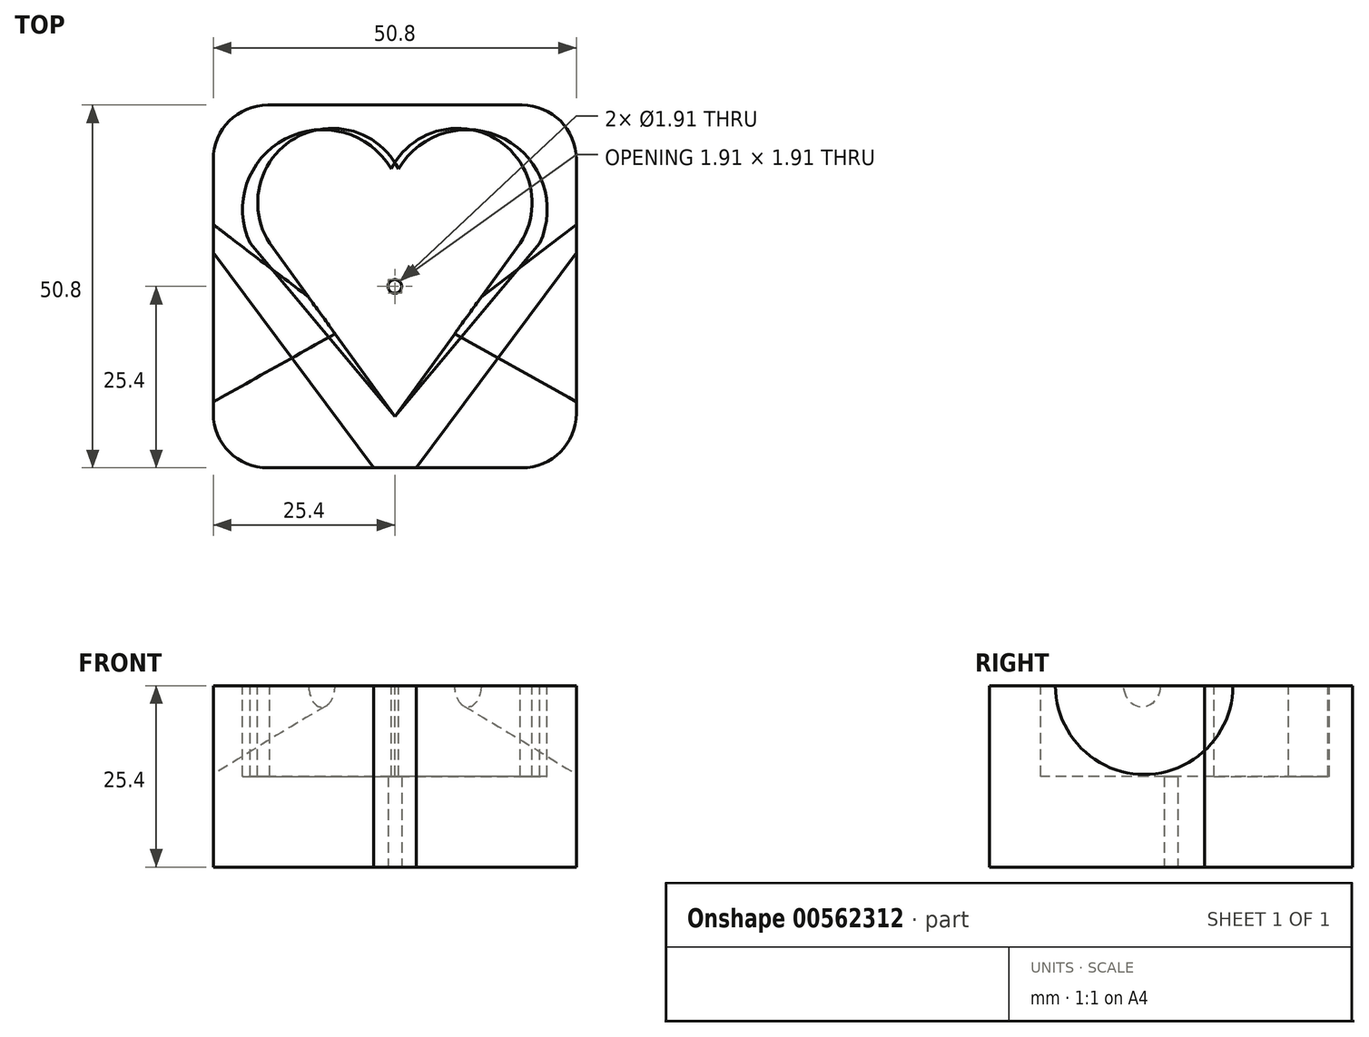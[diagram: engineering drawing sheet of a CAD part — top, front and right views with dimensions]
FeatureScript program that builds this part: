
annotation { "Feature Type Name" : "Feature", "Feature Type Description" : "" }
export const myFeature = defineFeature(function(context is Context, id is Id, definition is map)
    precondition{}
    {
        {
            var Q0;
            Q0=qCreatedBy(makeId("Top.planeOp"),FACE);
            var sketch = newSketch(context, id + "F0", { "sketchPlane" : qUnion([Q0])});
            skLineSegment(sketch, "E0.bottom", {"start": v(25.4, 25.4) * mm, "end": v(-25.4, 25.4) * mm});
            skLineSegment(sketch, "E0.top", {"start": v(25.4, -25.4) * mm, "end": v(-25.4, -25.4) * mm});
            skLineSegment(sketch, "E0.left", {"start": v(25.4, 25.4) * mm, "end": v(25.4, -25.4) * mm});
            skLineSegment(sketch, "E0.right", {"start": v(-25.4, 25.4) * mm, "end": v(-25.4, -25.4) * mm});
            skPoint(sketch, "E0.middle", {"position": v(0, 0) * mm});
            skSolve(sketch);
        }
        {
            var Q0;
            Q0=makeQuery(id+"F0.imprint","IMPRINT",FACE,{"disambiguationData":[TD([[makeQuery(id+"F0.imprint","IMPRINT",EDGE,{"derivedFrom":sQuery(id+"F0.wireOp",EDGE,"E0.bottom")}),1.0]])]});
            extrude(context, id + "F1", {"entities" : qUnion([Q0]), "depth" : 25.4 * mm, "offsetDistance" : 25.4 * mm});
        }
        {
            var Q0;
            Q0=makeQuery(id+"F1.opExtrude","CAP_FACE",FACE,{"disambiguationData":[OSD([sQuery(id+"F0.wireOp",EDGE,"E0.bottom"),sQuery(id+"F0.wireOp",EDGE,"E0.top"),sQuery(id+"F0.wireOp",EDGE,"E0.left"),sQuery(id+"F0.wireOp",EDGE,"E0.right")])],"isStart":false});
            var sketch = newSketch(context, id + "F2", { "sketchPlane" : qUnion([Q0])});
            skPoint(sketch, "E1.middle", {"position": v(0, 0) * mm});
            skPoint(sketch, "E2.start.orphan", {"position": v(0, 2.79) * mm});
            skPoint(sketch, "E3.end.orphan", {"position": v(14.02, 0) * mm});
            skPoint(sketch, "E4.end.orphan", {"position": v(-16.02, 0) * mm});
            skPoint(sketch, "E4.start.orphan", {"position": v(0, -21.13) * mm});
            skArc(sketch, "E5", {"start": v(-0.52, 16.47) * mm, "mid": v(-15.35, 20.66) * mm, "end": v(-20.27, 6.06) * mm});
            skArc(sketch, "E6", {"start": v(17.54, 6.06) * mm, "mid": v(13.98, 20.75) * mm, "end": v(-0.52, 16.47) * mm});
            skPoint(sketch, "E7.orphan", {"position": v(0, 6.06) * mm});
            skLineSegment(sketch, "E8", {"start": v(-20.27, 6.06) * mm, "end": v(0, -18.2) * mm});
            skLineSegment(sketch, "E9", {"start": v(17.54, 6.06) * mm, "end": v(0, -18.2) * mm});
            skSolve(sketch);
        }
        {
            var Q0;
            Q0 = qSketchRegion(id + "F2", true);
            extrude(context, id + "F3", {"entities" : qUnion([Q0]), "operationType" : NewBodyOperationType.REMOVE, "oppositeDirection" : true, "depth" : 12.7 * mm, "offsetDistance" : 25.4 * mm});
        }
        {
            var Q0;
            Q0=makeQuery(id+"F1.opExtrude","SWEPT_FACE",FACE,{"disambiguationData":[OSD([sQuery(id+"F0.wireOp",EDGE,"E0.left")])]});
            var sketch = newSketch(context, id + "F4", { "sketchPlane" : qUnion([Q0])});
            skLineSegment(sketch, "E10", {"start": v(-16.17, 25.4) * mm, "end": v(8.66, 25.4) * mm});
            skArc(sketch, "E11", {"start": v(-16.17, 25.4) * mm, "mid": v(-3.75, 12.97) * mm, "end": v(8.66, 25.4) * mm});
            skSolve(sketch);
        }
        {
            var Q0;
            Q0=makeQuery(id+"F3.boolean.opBoolean","COPY",FACE,{"derivedFrom":makeQuery(id+"F3.opExtrude","SWEPT_FACE",FACE,{"disambiguationData":[OSD([sQuery(id+"F2.wireOp",EDGE,"E9")])]})});
            var sketch = newSketch(context, id + "F5", { "sketchPlane" : qUnion([Q0])});
            skLineSegment(sketch, "E12", {"start": v(0.47, 25.4) * mm, "end": v(-5.87, 25.4) * mm});
            skArc(sketch, "E13", {"start": v(-5.87, 25.4) * mm, "mid": v(-2.7, 22.39) * mm, "end": v(0.47, 25.4) * mm});
            skSolve(sketch);
        }
        {
            var Q1;
            Q1=makeQuery(id+"F4.imprint","IMPRINT",FACE,{"disambiguationData":[TD([[makeQuery(id+"F4.imprint","IMPRINT",EDGE,{"derivedFrom":sQuery(id+"F4.wireOp",EDGE,"E10")}),1.0]])]});
            var Q2;
            Q2=makeQuery(id+"F5.imprint","IMPRINT",FACE,{"disambiguationData":[TD([[makeQuery(id+"F5.imprint","IMPRINT",EDGE,{"derivedFrom":sQuery(id+"F5.wireOp",EDGE,"E12")}),-1.0]])]});
            loft(context, id + "F6", {"operationType" : NewBodyOperationType.REMOVE, "sheetProfilesArray" : [{ "sheetProfileEntities" : qUnion([Q1]) }, { "sheetProfileEntities" : qUnion([Q2]) }]});
        }
        {
            var Q0;
            Q0=makeQuery(id+"F1.opExtrude","CAP_FACE",FACE,{"disambiguationData":[OSD([sQuery(id+"F0.wireOp",EDGE,"E0.bottom"),sQuery(id+"F0.wireOp",EDGE,"E0.top"),sQuery(id+"F0.wireOp",EDGE,"E0.left"),sQuery(id+"F0.wireOp",EDGE,"E0.right")])],"isStart":true});
            var sketch = newSketch(context, id + "F7", { "sketchPlane" : qUnion([Q0])});
            skCircle(sketch, "E14", {"center": v(0, 0) * mm, "radius": 0.95 * mm});
            skSolve(sketch);
        }
        {
            var Q0;
            Q0=makeQuery(id+"F7.imprint","IMPRINT",FACE,{"disambiguationData":[TD([[makeQuery(id+"F7.imprint","IMPRINT",EDGE,{"derivedFrom":sQuery(id+"F7.wireOp",EDGE,"E14")}),1.0]])]});
            extrude(context, id + "F8", {"entities" : qUnion([Q0]), "operationType" : NewBodyOperationType.REMOVE, "oppositeDirection" : true, "depth" : 25.4 * mm, "offsetDistance" : 25.4 * mm});
        }
        {
            var Q0;
            Q0=makeQuery(id+"F1.opExtrude","CAP_FACE",FACE,{"disambiguationData":[OSD([sQuery(id+"F0.wireOp",EDGE,"E0.bottom"),sQuery(id+"F0.wireOp",EDGE,"E0.top"),sQuery(id+"F0.wireOp",EDGE,"E0.left"),sQuery(id+"F0.wireOp",EDGE,"E0.right")])],"isStart":false});
            var sketch = newSketch(context, id + "F9", { "sketchPlane" : qUnion([Q0])});
            skLineSegment(sketch, "E15", {"start": v(-25.4, 4.72) * mm, "end": v(-2.97, -25.4) * mm});
            skLineSegment(sketch, "E16", {"start": v(-2.97, -25.4) * mm, "end": v(-25.4, -25.4) * mm});
            skLineSegment(sketch, "E17", {"start": v(-25.4, -25.4) * mm, "end": v(-25.4, 4.72) * mm});
            skSolve(sketch);
        }
        {
            var Q0;
            Q0=makeQuery(id+"F9.imprint","IMPRINT",FACE,{"disambiguationData":[TD([[makeQuery(id+"F9.imprint","IMPRINT",EDGE,{"derivedFrom":sQuery(id+"F9.wireOp",EDGE,"E15")}),-1.0]])]});
            extrude(context, id + "F10", {"entities" : qUnion([Q0]), "operationType" : NewBodyOperationType.REMOVE, "oppositeDirection" : true, "depth" : 25.4 * mm, "offsetDistance" : 25.4 * mm});
        }
        {
            var Q0;
            Q0=makeQuery(id+"F10.boolean.opBoolean","COPY",EDGE,{"derivedFrom":makeQuery(id+"F10.opExtrude","SWEPT_EDGE",EDGE,{"disambiguationData":[OSD([sQuery(id+"F0.wireOp",EDGE,"E0.right"),sQuery(id+"F9.wireOp",EDGE,"E15"),sQuery(id+"F9.wireOp",EDGE,"E17")])]})});
            var Q1;
            Q1=makeQuery(id+"F1.opExtrude","SWEPT_EDGE",EDGE,{"disambiguationData":[OSD([sQuery(id+"F0.wireOp",EDGE,"E0.bottom"),sQuery(id+"F0.wireOp",EDGE,"E0.right")])]});
            var Q2;
            Q2=makeQuery(id+"F10.boolean.opBoolean","COPY",EDGE,{"derivedFrom":makeQuery(id+"F10.opExtrude","SWEPT_EDGE",EDGE,{"disambiguationData":[OSD([sQuery(id+"F0.wireOp",EDGE,"E0.top"),sQuery(id+"F9.wireOp",EDGE,"E15"),sQuery(id+"F9.wireOp",EDGE,"E16")])]})});
            var Q3;
            Q3=makeQuery(id+"F1.opExtrude","SWEPT_EDGE",EDGE,{"disambiguationData":[OSD([sQuery(id+"F0.wireOp",EDGE,"E0.top"),sQuery(id+"F0.wireOp",EDGE,"E0.left")])]});
            var Q4;
            Q4=makeQuery(id+"F1.opExtrude","SWEPT_EDGE",EDGE,{"disambiguationData":[OSD([sQuery(id+"F0.wireOp",EDGE,"E0.bottom"),sQuery(id+"F0.wireOp",EDGE,"E0.left")])]});
            fillet(context, id + "F11", {"entities" : qUnion([Q0, Q1, Q2, Q3, Q4]), "radius" : 7.62 * mm, "tangentPropagation" : true, "allowEdgeOverflow" : false});
        }
        {
            var Q0;
            Q0=makeQuery(id+"F1.opExtrude","SWEPT_BODY",BODY,{"disambiguationData":[OSD([sQuery(id+"F0.wireOp",EDGE,"E0.bottom"),sQuery(id+"F0.wireOp",EDGE,"E0.top"),sQuery(id+"F0.wireOp",EDGE,"E0.left"),sQuery(id+"F0.wireOp",EDGE,"E0.right")])]});
            var Q1;
            Q1=qCreatedBy(makeId("Right.planeOp"),FACE);
            mirror(context, id + "F12", {"entities" : qUnion([Q0]), "mirrorPlane" : qUnion([Q1])});
        }
    });
